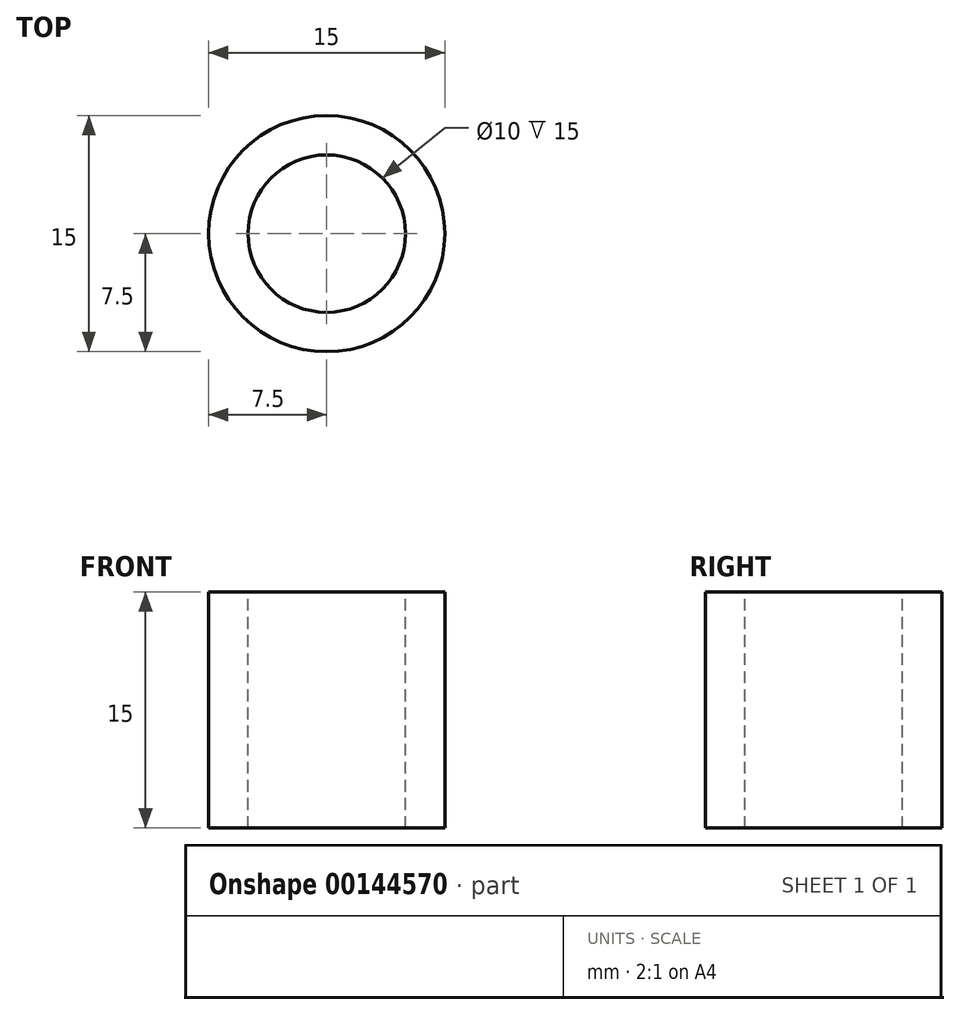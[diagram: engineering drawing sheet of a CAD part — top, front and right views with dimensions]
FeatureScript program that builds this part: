
annotation { "Feature Type Name" : "Feature", "Feature Type Description" : "" }
export const myFeature = defineFeature(function(context is Context, id is Id, definition is map)
    precondition{}
    {
        {
            var Q0;
            Q0=qCreatedBy(makeId("Top.planeOp"),FACE);
            var sketch = newSketch(context, id + "F0", { "sketchPlane" : qUnion([Q0])});
            skCircle(sketch, "E0", {"center": v(0, 0) * mm, "radius": 7.5 * mm});
            skSolve(sketch);
        }
        {
            var Q0;
            Q0=makeQuery(id+"F0.imprint","IMPRINT",FACE,{"disambiguationData":[TD([[makeQuery(id+"F0.imprint","IMPRINT",EDGE,{"derivedFrom":sQuery(id+"F0.wireOp",EDGE,"E0")}),1.0]])]});
            extrude(context, id + "F1", {"entities" : qUnion([Q0]), "endBound" : BoundingType.SYMMETRIC, "depth" : 15 * mm});
        }
        {
            var Q0;
            Q0=makeQuery(id+"F1.opExtrude","CAP_FACE",FACE,{"disambiguationData":[OSD([sQuery(id+"F0.wireOp",EDGE,"E0")])],"isStart":false});
            var sketch = newSketch(context, id + "F2", { "sketchPlane" : qUnion([Q0])});
            skPoint(sketch, "E1", {"position": v(0, 0) * mm});
            skSolve(sketch);
        }
        {
            var Q0;
            Q0=sQuery(id+"F2.wireOp",VERTEX,"E1");
            var Q1;
            Q1=makeQuery(id+"F1.opExtrude","SWEPT_BODY",BODY,{"disambiguationData":[OSD([sQuery(id+"F0.wireOp",EDGE,"E0")])]});
            hole(context, id + "F3", {"style" : HoleStyle.SIMPLE, "endStyle" : HoleEndStyle.BLIND, "holeDiameter" : 10 * mm, "holeDepth" : 25 * mm, "locations" : qUnion([Q0]), "scope" : qUnion([Q1])});
        }
    });
